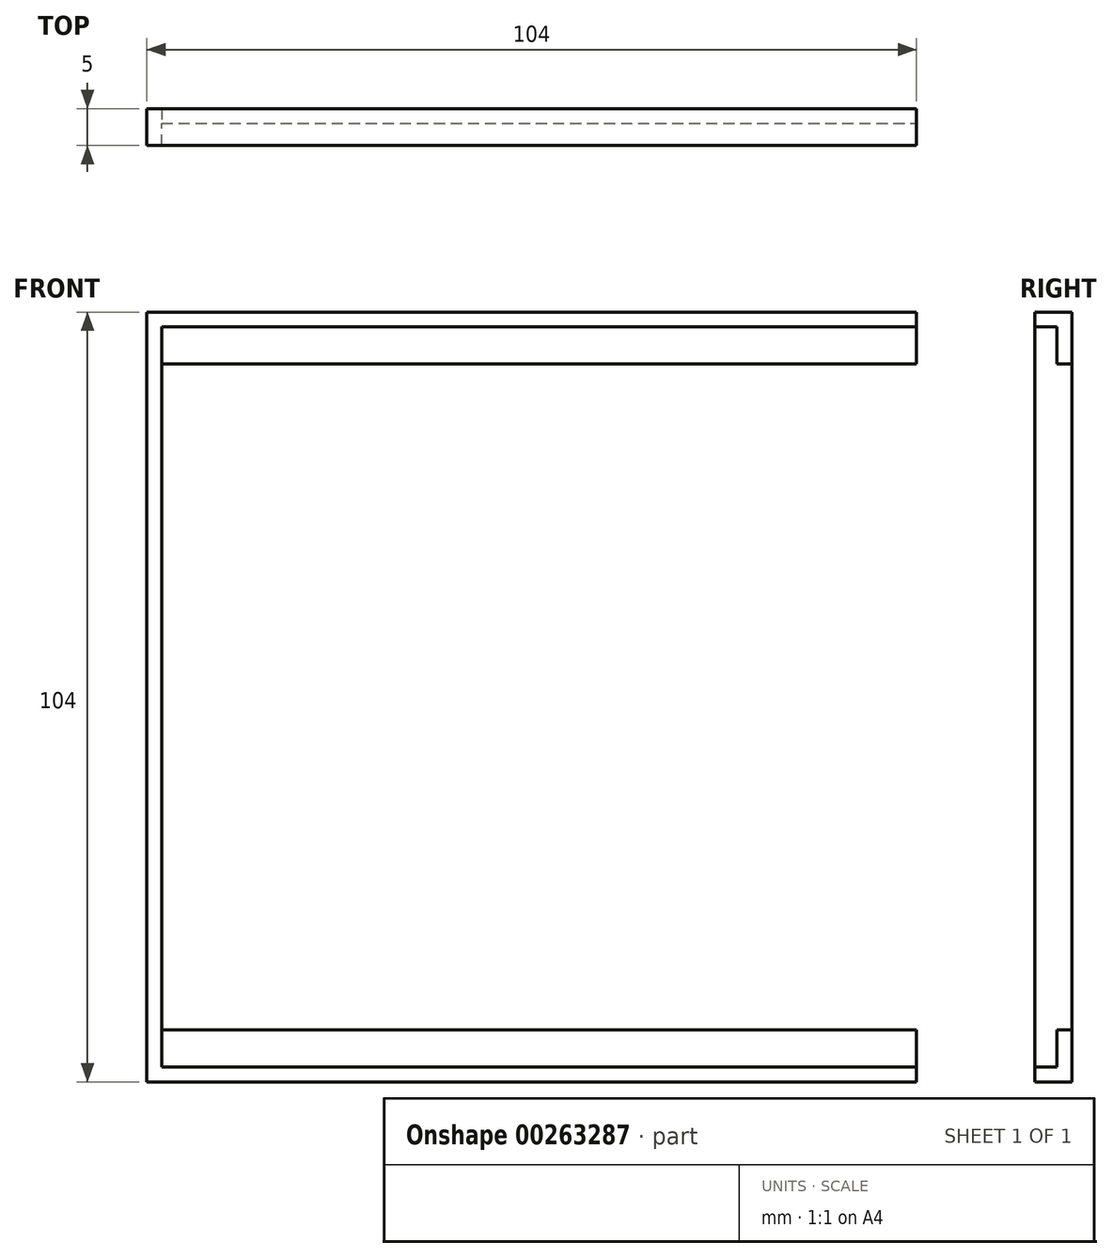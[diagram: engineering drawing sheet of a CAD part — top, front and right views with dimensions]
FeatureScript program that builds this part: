
annotation { "Feature Type Name" : "Feature", "Feature Type Description" : "" }
export const myFeature = defineFeature(function(context is Context, id is Id, definition is map)
    precondition{}
    {
        {
            var Q0;
            Q0=qCreatedBy(makeId("Front.planeOp"),FACE);
            var sketch = newSketch(context, id + "F0", { "sketchPlane" : qUnion([Q0])});
            skLineSegment(sketch, "E0.bottom", {"start": v(52, -52) * mm, "end": v(-52, -52) * mm});
            skLineSegment(sketch, "E0.top", {"start": v(52, 52) * mm, "end": v(-52, 52) * mm});
            skLineSegment(sketch, "E0.left", {"start": v(52, -52) * mm, "end": v(52, 52) * mm});
            skLineSegment(sketch, "E0.right", {"start": v(-52, -52) * mm, "end": v(-52, 52) * mm});
            skPoint(sketch, "E0.middle", {"position": v(0, 0) * mm});
            skSolve(sketch);
        }
        {
            var Q0;
            Q0 = qSketchRegion(id + "F0", true);
            extrude(context, id + "F1", {"entities" : qUnion([Q0]), "depth" : 2 * mm});
        }
        {
            var Q0;
            Q0=makeQuery(id+"F1.opExtrude","CAP_FACE",FACE,{"disambiguationData":[OSD([sQuery(id+"F0.wireOp",EDGE,"E0.bottom"),sQuery(id+"F0.wireOp",EDGE,"E0.top"),sQuery(id+"F0.wireOp",EDGE,"E0.left"),sQuery(id+"F0.wireOp",EDGE,"E0.right")])],"isStart":false});
            var sketch = newSketch(context, id + "F2", { "sketchPlane" : qUnion([Q0])});
            skLineSegment(sketch, "E1.bottom", {"start": v(52, 52) * mm, "end": v(-52, 52) * mm});
            skLineSegment(sketch, "E1.top", {"start": v(52, 50) * mm, "end": v(-52, 50) * mm});
            skLineSegment(sketch, "E1.left", {"start": v(52, 52) * mm, "end": v(52, 50) * mm});
            skLineSegment(sketch, "E1.right", {"start": v(-52, 52) * mm, "end": v(-52, 50) * mm});
            skSolve(sketch);
        }
        {
            var Q0;
            Q0 = qSketchRegion(id + "F2", true);
            extrude(context, id + "F3", {"entities" : qUnion([Q0]), "operationType" : NewBodyOperationType.ADD, "depth" : 3 * mm});
        }
        {
            var Q0;
            Q0=makeQuery(id+"F1.opExtrude","CAP_FACE",FACE,{"disambiguationData":[OSD([sQuery(id+"F0.wireOp",EDGE,"E0.bottom"),sQuery(id+"F0.wireOp",EDGE,"E0.top"),sQuery(id+"F0.wireOp",EDGE,"E0.left"),sQuery(id+"F0.wireOp",EDGE,"E0.right")])],"isStart":false});
            var sketch = newSketch(context, id + "F4", { "sketchPlane" : qUnion([Q0])});
            skLineSegment(sketch, "E2.bottom", {"start": v(-52, -52) * mm, "end": v(-50, -52) * mm});
            skLineSegment(sketch, "E2.top", {"start": v(-52, 50) * mm, "end": v(-50, 50) * mm});
            skLineSegment(sketch, "E2.left", {"start": v(-52, -52) * mm, "end": v(-52, 50) * mm});
            skLineSegment(sketch, "E2.right", {"start": v(-50, -52) * mm, "end": v(-50, 50) * mm});
            skSolve(sketch);
        }
        {
            var Q0;
            Q0 = qSketchRegion(id + "F4", true);
            extrude(context, id + "F5", {"entities" : qUnion([Q0]), "operationType" : NewBodyOperationType.ADD, "depth" : 3 * mm});
        }
        {
            var Q0;
            Q0=makeQuery(id+"F1.opExtrude","CAP_FACE",FACE,{"disambiguationData":[OSD([sQuery(id+"F0.wireOp",EDGE,"E0.bottom"),sQuery(id+"F0.wireOp",EDGE,"E0.top"),sQuery(id+"F0.wireOp",EDGE,"E0.left"),sQuery(id+"F0.wireOp",EDGE,"E0.right")])],"isStart":false});
            var sketch = newSketch(context, id + "F6", { "sketchPlane" : qUnion([Q0])});
            skLineSegment(sketch, "E3.bottom", {"start": v(-50, -52) * mm, "end": v(52, -52) * mm});
            skLineSegment(sketch, "E3.top", {"start": v(-50, -50) * mm, "end": v(52, -50) * mm});
            skLineSegment(sketch, "E3.left", {"start": v(-50, -52) * mm, "end": v(-50, -50) * mm});
            skLineSegment(sketch, "E3.right", {"start": v(52, -52) * mm, "end": v(52, -50) * mm});
            skSolve(sketch);
        }
        {
            var Q0;
            Q0 = qSketchRegion(id + "F6", true);
            extrude(context, id + "F7", {"entities" : qUnion([Q0]), "operationType" : NewBodyOperationType.ADD, "depth" : 3 * mm});
        }
        {
            var Q0;
            Q0=makeQuery(id+"F1.opExtrude","CAP_FACE",FACE,{"disambiguationData":[OSD([sQuery(id+"F0.wireOp",EDGE,"E0.bottom"),sQuery(id+"F0.wireOp",EDGE,"E0.top"),sQuery(id+"F0.wireOp",EDGE,"E0.left"),sQuery(id+"F0.wireOp",EDGE,"E0.right")])],"isStart":false});
            var sketch = newSketch(context, id + "F8", { "sketchPlane" : qUnion([Q0])});
            skLineSegment(sketch, "E4.bottom", {"start": v(-50, 50) * mm, "end": v(52, 50) * mm});
            skLineSegment(sketch, "E4.top", {"start": v(-50, 45) * mm, "end": v(52, 45) * mm});
            skLineSegment(sketch, "E4.left", {"start": v(-50, 50) * mm, "end": v(-50, 45) * mm});
            skLineSegment(sketch, "E4.right", {"start": v(52, 50) * mm, "end": v(52, 45) * mm});
            skSolve(sketch);
        }
        {
            var Q0;
            Q0=makeQuery(id+"F1.opExtrude","CAP_FACE",FACE,{"disambiguationData":[OSD([sQuery(id+"F0.wireOp",EDGE,"E0.bottom"),sQuery(id+"F0.wireOp",EDGE,"E0.top"),sQuery(id+"F0.wireOp",EDGE,"E0.left"),sQuery(id+"F0.wireOp",EDGE,"E0.right")])],"isStart":false});
            var sketch = newSketch(context, id + "F9", { "sketchPlane" : qUnion([Q0])});
            skLineSegment(sketch, "E5.bottom", {"start": v(-50, -50) * mm, "end": v(52, -50) * mm});
            skLineSegment(sketch, "E5.top", {"start": v(-50, -45) * mm, "end": v(52, -45) * mm});
            skLineSegment(sketch, "E5.left", {"start": v(-50, -50) * mm, "end": v(-50, -45) * mm});
            skLineSegment(sketch, "E5.right", {"start": v(52, -50) * mm, "end": v(52, -45) * mm});
            skSolve(sketch);
        }
        {
            var Q0;
            Q0=makeQuery(id+"F1.opExtrude","CAP_FACE",FACE,{"disambiguationData":[OSD([sQuery(id+"F0.wireOp",EDGE,"E0.bottom"),sQuery(id+"F0.wireOp",EDGE,"E0.top"),sQuery(id+"F0.wireOp",EDGE,"E0.left"),sQuery(id+"F0.wireOp",EDGE,"E0.right")])],"isStart":false});
            var sketch = newSketch(context, id + "F10", { "sketchPlane" : qUnion([Q0])});
            skLineSegment(sketch, "E6.bottom", {"start": v(-50, 45) * mm, "end": v(52, 45) * mm});
            skLineSegment(sketch, "E6.top", {"start": v(-50, -45) * mm, "end": v(52, -45) * mm});
            skLineSegment(sketch, "E6.left", {"start": v(-50, 45) * mm, "end": v(-50, -45) * mm});
            skLineSegment(sketch, "E6.right", {"start": v(52, 45) * mm, "end": v(52, -45) * mm});
            skSolve(sketch);
        }
        {
            var Q0;
            Q0 = qSketchRegion(id + "F10", true);
            extrude(context, id + "F11", {"entities" : qUnion([Q0]), "operationType" : NewBodyOperationType.REMOVE, "oppositeDirection" : true, "depth" : 25 * mm});
        }
    });
